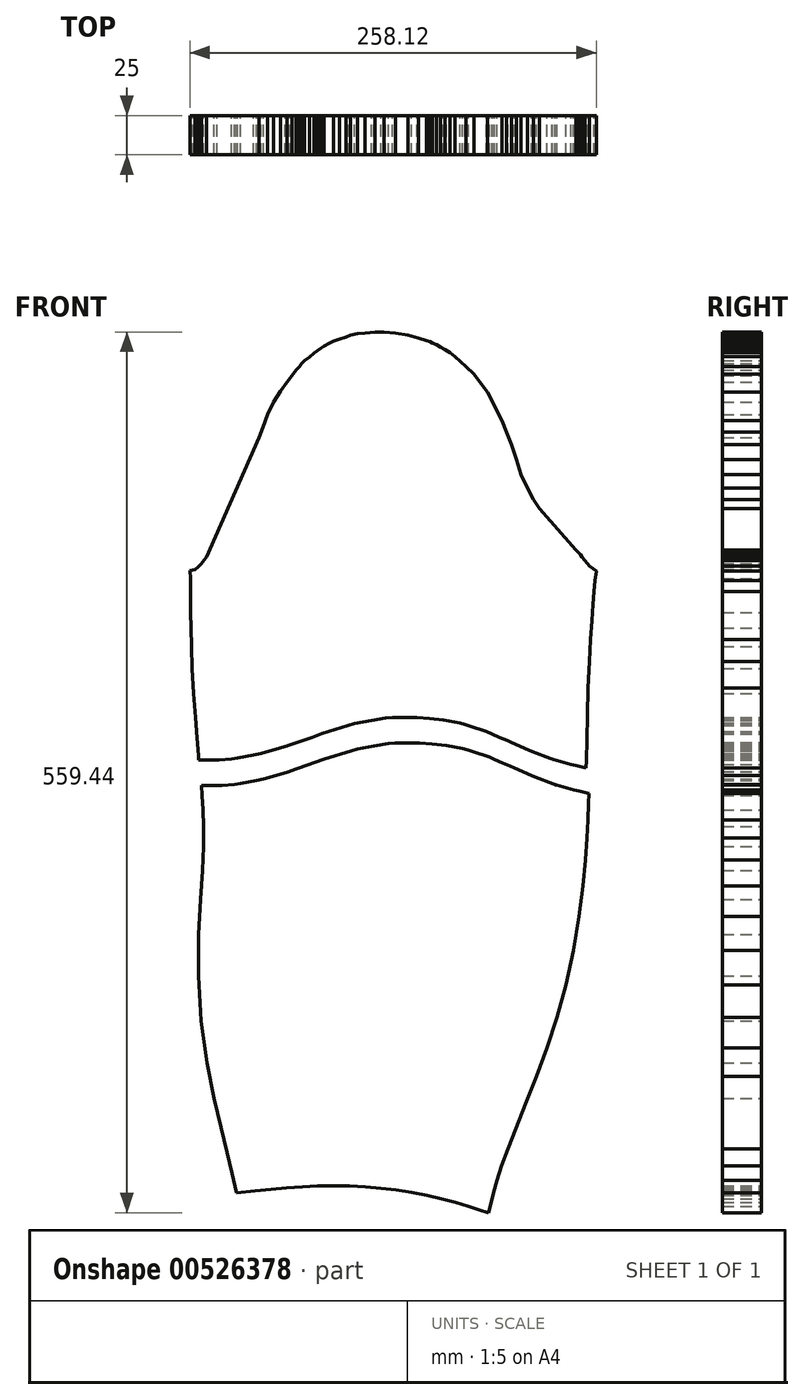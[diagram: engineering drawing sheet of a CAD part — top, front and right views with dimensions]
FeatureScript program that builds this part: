
annotation { "Feature Type Name" : "Feature", "Feature Type Description" : "" }
export const myFeature = defineFeature(function(context is Context, id is Id, definition is map)
    precondition{}
    {
        {
            var Q0;
            Q0=qCreatedBy(makeId("Front.planeOp"),FACE);
            var sketch = newSketch(context, id + "F0", { "sketchPlane" : qUnion([Q0])});
            skLineSegment(sketch, "E0", {"start": v(-129.06, 127.99) * mm, "end": v(-125.78, 128.92) * mm});
            skLineSegment(sketch, "E1", {"start": v(-125.78, 128.92) * mm, "end": v(-123.74, 130.52) * mm});
            skLineSegment(sketch, "E2", {"start": v(-123.74, 130.52) * mm, "end": v(-121.67, 132.71) * mm});
            skLineSegment(sketch, "E3", {"start": v(-121.67, 132.71) * mm, "end": v(-119.92, 134.96) * mm});
            skLineSegment(sketch, "E4", {"start": v(-119.92, 134.96) * mm, "end": v(-118.45, 136.86) * mm});
            skLineSegment(sketch, "E5", {"start": v(-118.45, 136.86) * mm, "end": v(-85.06, 212.65) * mm});
            skLineSegment(sketch, "E6", {"start": v(-85.06, 212.65) * mm, "end": v(-82.6, 219.33) * mm});
            skLineSegment(sketch, "E7", {"start": v(-82.6, 219.33) * mm, "end": v(-79.7, 227.1) * mm});
            skLineSegment(sketch, "E8", {"start": v(-79.7, 227.1) * mm, "end": v(-75.87, 235.03) * mm});
            skLineSegment(sketch, "E9", {"start": v(-75.87, 235.03) * mm, "end": v(-71.47, 242.22) * mm});
            skLineSegment(sketch, "E10", {"start": v(-71.47, 242.22) * mm, "end": v(-67.32, 247.98) * mm});
            skLineSegment(sketch, "E11", {"start": v(-67.32, 247.98) * mm, "end": v(-64.18, 252.12) * mm});
            skLineSegment(sketch, "E12", {"start": v(-64.18, 252.12) * mm, "end": v(-61.7, 255.53) * mm});
            skLineSegment(sketch, "E13", {"start": v(-61.7, 255.53) * mm, "end": v(-59.4, 257.84) * mm});
            skLineSegment(sketch, "E14", {"start": v(-59.4, 257.84) * mm, "end": v(-58.19, 259.5) * mm});
            skLineSegment(sketch, "E15", {"start": v(-58.19, 259.5) * mm, "end": v(-56.4, 261.46) * mm});
            skLineSegment(sketch, "E16", {"start": v(-56.4, 261.46) * mm, "end": v(-53.2, 263.83) * mm});
            skLineSegment(sketch, "E17", {"start": v(-53.2, 263.83) * mm, "end": v(-50.06, 266.24) * mm});
            skLineSegment(sketch, "E18", {"start": v(-50.06, 266.24) * mm, "end": v(-48.03, 267.92) * mm});
            skLineSegment(sketch, "E19", {"start": v(-48.03, 267.92) * mm, "end": v(-45.8, 269.31) * mm});
            skLineSegment(sketch, "E20", {"start": v(-45.8, 269.31) * mm, "end": v(-43.72, 270.77) * mm});
            skLineSegment(sketch, "E21", {"start": v(-43.72, 270.77) * mm, "end": v(-40.37, 272.52) * mm});
            skLineSegment(sketch, "E22", {"start": v(-40.37, 272.52) * mm, "end": v(-37.71, 273.92) * mm});
            skLineSegment(sketch, "E23", {"start": v(-37.71, 273.92) * mm, "end": v(-33.9, 275.3) * mm});
            skLineSegment(sketch, "E24", {"start": v(-33.9, 275.3) * mm, "end": v(-30.01, 276.47) * mm});
            skLineSegment(sketch, "E25", {"start": v(-30.01, 276.47) * mm, "end": v(-27.04, 277.54) * mm});
            skLineSegment(sketch, "E26", {"start": v(-27.04, 277.54) * mm, "end": v(-22.6, 278.6) * mm});
            skLineSegment(sketch, "E27", {"start": v(-22.6, 278.6) * mm, "end": v(-17.94, 279.04) * mm});
            skLineSegment(sketch, "E28", {"start": v(-17.94, 279.04) * mm, "end": v(-11.4, 279.5) * mm});
            skLineSegment(sketch, "E29", {"start": v(-11.4, 279.5) * mm, "end": v(-5.8, 279.72) * mm});
            skLineSegment(sketch, "E30", {"start": v(-5.8, 279.72) * mm, "end": v(1.6, 279.03) * mm});
            skLineSegment(sketch, "E31", {"start": v(1.6, 279.03) * mm, "end": v(9.41, 277.6) * mm});
            skLineSegment(sketch, "E32", {"start": v(9.41, 277.6) * mm, "end": v(16.28, 275.7) * mm});
            skLineSegment(sketch, "E33", {"start": v(16.28, 275.7) * mm, "end": v(21.23, 274.15) * mm});
            skLineSegment(sketch, "E34", {"start": v(21.23, 274.15) * mm, "end": v(23.5, 273.55) * mm});
            skLineSegment(sketch, "E35", {"start": v(23.5, 273.55) * mm, "end": v(25.19, 272.62) * mm});
            skLineSegment(sketch, "E36", {"start": v(25.19, 272.62) * mm, "end": v(27.5, 271.6) * mm});
            skLineSegment(sketch, "E37", {"start": v(27.5, 271.6) * mm, "end": v(30.25, 269.98) * mm});
            skLineSegment(sketch, "E38", {"start": v(30.25, 269.98) * mm, "end": v(32.91, 268.54) * mm});
            skLineSegment(sketch, "E39", {"start": v(32.91, 268.54) * mm, "end": v(36.27, 266.46) * mm});
            skLineSegment(sketch, "E40", {"start": v(36.27, 266.46) * mm, "end": v(39.3, 263.93) * mm});
            skLineSegment(sketch, "E41", {"start": v(39.3, 263.93) * mm, "end": v(46.3, 257.73) * mm});
            skLineSegment(sketch, "E42", {"start": v(46.3, 257.73) * mm, "end": v(51.38, 252.95) * mm});
            skLineSegment(sketch, "E43", {"start": v(51.38, 252.95) * mm, "end": v(55.72, 247.02) * mm});
            skLineSegment(sketch, "E44", {"start": v(55.72, 247.02) * mm, "end": v(59.84, 241.45) * mm});
            skLineSegment(sketch, "E45", {"start": v(59.84, 241.45) * mm, "end": v(69.25, 223.53) * mm});
            skLineSegment(sketch, "E46", {"start": v(69.25, 223.53) * mm, "end": v(71.89, 216.2) * mm});
            skLineSegment(sketch, "E47", {"start": v(71.89, 216.2) * mm, "end": v(75.36, 208) * mm});
            skLineSegment(sketch, "E48", {"start": v(75.36, 208) * mm, "end": v(78.39, 198.63) * mm});
            skLineSegment(sketch, "E49", {"start": v(78.39, 198.63) * mm, "end": v(81.28, 188.97) * mm});
            skLineSegment(sketch, "E50", {"start": v(81.28, 188.97) * mm, "end": v(85.37, 180.55) * mm});
            skLineSegment(sketch, "E51", {"start": v(85.37, 180.55) * mm, "end": v(89.27, 173.34) * mm});
            skLineSegment(sketch, "E52", {"start": v(89.27, 173.34) * mm, "end": v(93, 167.63) * mm});
            skLineSegment(sketch, "E53", {"start": v(93, 167.63) * mm, "end": v(116.08, 141.22) * mm});
            skLineSegment(sketch, "E54", {"start": v(116.08, 141.22) * mm, "end": v(117.67, 139.44) * mm});
            skLineSegment(sketch, "E55", {"start": v(117.67, 139.44) * mm, "end": v(118.96, 138.2) * mm});
            skLineSegment(sketch, "E56", {"start": v(118.96, 138.2) * mm, "end": v(120.13, 136.65) * mm});
            skLineSegment(sketch, "E57", {"start": v(120.13, 136.65) * mm, "end": v(121.99, 134.64) * mm});
            skLineSegment(sketch, "E58", {"start": v(121.99, 134.64) * mm, "end": v(124.73, 131.11) * mm});
            skLineSegment(sketch, "E59", {"start": v(124.73, 131.11) * mm, "end": v(129.06, 127.9) * mm});
            skLineSegment(sketch, "E60", {"start": v(129.06, 127.9) * mm, "end": v(128.28, 121.94) * mm});
            skLineSegment(sketch, "E61", {"start": v(128.28, 121.94) * mm, "end": v(127.6, 114.85) * mm});
            skLineSegment(sketch, "E62", {"start": v(127.6, 114.85) * mm, "end": v(126.92, 106.4) * mm});
            skLineSegment(sketch, "E63", {"start": v(126.92, 106.4) * mm, "end": v(126.18, 96.34) * mm});
            skLineSegment(sketch, "E64", {"start": v(126.18, 96.34) * mm, "end": v(125.4, 84.41) * mm});
            skLineSegment(sketch, "E65", {"start": v(125.4, 84.41) * mm, "end": v(124.62, 70.26) * mm});
            skLineSegment(sketch, "E66", {"start": v(124.62, 70.26) * mm, "end": v(123.94, 53.44) * mm});
            skLineSegment(sketch, "E67", {"start": v(123.94, 53.44) * mm, "end": v(123.45, 36.05) * mm});
            skLineSegment(sketch, "E68", {"start": v(123.45, 36.05) * mm, "end": v(123.1, 20.74) * mm});
            skLineSegment(sketch, "E69", {"start": v(123.1, 20.74) * mm, "end": v(122.77, 7.64) * mm});
            skLineSegment(sketch, "E70", {"start": v(122.77, 7.64) * mm, "end": v(122.6, 2.87) * mm});
            skLineSegment(sketch, "E71", {"start": v(122.6, 2.87) * mm, "end": v(116.26, 4.18) * mm});
            skLineSegment(sketch, "E72", {"start": v(116.26, 4.18) * mm, "end": v(113.1, 4.8) * mm});
            skLineSegment(sketch, "E73", {"start": v(113.1, 4.8) * mm, "end": v(102, 8.01) * mm});
            skLineSegment(sketch, "E74", {"start": v(102, 8.01) * mm, "end": v(101.15, 8.25) * mm});
            skLineSegment(sketch, "E75", {"start": v(101.15, 8.25) * mm, "end": v(100.98, 8.32) * mm});
            skLineSegment(sketch, "E76", {"start": v(100.98, 8.32) * mm, "end": v(100.06, 8.68) * mm});
            skLineSegment(sketch, "E77", {"start": v(100.06, 8.68) * mm, "end": v(88.25, 13.28) * mm});
            skLineSegment(sketch, "E78", {"start": v(88.25, 13.28) * mm, "end": v(86.15, 14.09) * mm});
            skLineSegment(sketch, "E79", {"start": v(86.15, 14.09) * mm, "end": v(75.3, 18.88) * mm});
            skLineSegment(sketch, "E80", {"start": v(75.3, 18.88) * mm, "end": v(72.52, 20.08) * mm});
            skLineSegment(sketch, "E81", {"start": v(72.52, 20.08) * mm, "end": v(67.7, 22.18) * mm});
            skLineSegment(sketch, "E82", {"start": v(67.7, 22.18) * mm, "end": v(62.7, 24.37) * mm});
            skLineSegment(sketch, "E83", {"start": v(62.7, 24.37) * mm, "end": v(59.36, 25.76) * mm});
            skLineSegment(sketch, "E84", {"start": v(59.36, 25.76) * mm, "end": v(48.53, 29.38) * mm});
            skLineSegment(sketch, "E85", {"start": v(48.53, 29.38) * mm, "end": v(45.64, 30.34) * mm});
            skLineSegment(sketch, "E86", {"start": v(45.64, 30.34) * mm, "end": v(42.36, 31.17) * mm});
            skLineSegment(sketch, "E87", {"start": v(42.36, 31.17) * mm, "end": v(32.12, 33.1) * mm});
            skLineSegment(sketch, "E88", {"start": v(32.12, 33.1) * mm, "end": v(23.04, 34.23) * mm});
            skLineSegment(sketch, "E89", {"start": v(23.04, 34.23) * mm, "end": v(15.13, 34.8) * mm});
            skLineSegment(sketch, "E90", {"start": v(15.13, 34.8) * mm, "end": v(-0.5, 34.69) * mm});
            skLineSegment(sketch, "E91", {"start": v(-0.5, 34.69) * mm, "end": v(-4.82, 34.6) * mm});
            skLineSegment(sketch, "E92", {"start": v(-4.82, 34.6) * mm, "end": v(-13.8, 32.87) * mm});
            skLineSegment(sketch, "E93", {"start": v(-13.8, 32.87) * mm, "end": v(-24.33, 30.99) * mm});
            skLineSegment(sketch, "E94", {"start": v(-24.33, 30.99) * mm, "end": v(-28.64, 29.75) * mm});
            skLineSegment(sketch, "E95", {"start": v(-28.64, 29.75) * mm, "end": v(-45.2, 24.49) * mm});
            skLineSegment(sketch, "E96", {"start": v(-45.2, 24.49) * mm, "end": v(-51.53, 22.25) * mm});
            skLineSegment(sketch, "E97", {"start": v(-51.53, 22.25) * mm, "end": v(-66.86, 16.9) * mm});
            skLineSegment(sketch, "E98", {"start": v(-66.86, 16.9) * mm, "end": v(-67.43, 16.71) * mm});
            skLineSegment(sketch, "E99", {"start": v(-67.43, 16.71) * mm, "end": v(-68.62, 16.33) * mm});
            skLineSegment(sketch, "E100", {"start": v(-68.62, 16.33) * mm, "end": v(-71.7, 15.5) * mm});
            skLineSegment(sketch, "E101", {"start": v(-71.7, 15.5) * mm, "end": v(-84, 12.04) * mm});
            skLineSegment(sketch, "E102", {"start": v(-84, 12.04) * mm, "end": v(-88.47, 11.04) * mm});
            skLineSegment(sketch, "E103", {"start": v(-88.47, 11.04) * mm, "end": v(-98.66, 9.15) * mm});
            skLineSegment(sketch, "E104", {"start": v(-98.66, 9.15) * mm, "end": v(-102.44, 8.55) * mm});
            skLineSegment(sketch, "E105", {"start": v(-102.44, 8.55) * mm, "end": v(-110.4, 7.93) * mm});
            skLineSegment(sketch, "E106", {"start": v(-110.4, 7.93) * mm, "end": v(-113.6, 7.68) * mm});
            skLineSegment(sketch, "E107", {"start": v(-113.6, 7.68) * mm, "end": v(-116.64, 7.7) * mm});
            skLineSegment(sketch, "E108", {"start": v(-116.64, 7.7) * mm, "end": v(-123.46, 7.78) * mm});
            skLineSegment(sketch, "E109", {"start": v(-123.46, 7.78) * mm, "end": v(-123.66, 10.72) * mm});
            skLineSegment(sketch, "E110", {"start": v(-123.66, 10.72) * mm, "end": v(-124.49, 21.76) * mm});
            skLineSegment(sketch, "E111", {"start": v(-124.49, 21.76) * mm, "end": v(-125.5, 34.65) * mm});
            skLineSegment(sketch, "E112", {"start": v(-125.5, 34.65) * mm, "end": v(-126.62, 50.2) * mm});
            skLineSegment(sketch, "E113", {"start": v(-126.62, 50.2) * mm, "end": v(-127.52, 66.05) * mm});
            skLineSegment(sketch, "E114", {"start": v(-127.52, 66.05) * mm, "end": v(-128.1, 79.86) * mm});
            skLineSegment(sketch, "E115", {"start": v(-128.1, 79.86) * mm, "end": v(-128.43, 91.56) * mm});
            skLineSegment(sketch, "E116", {"start": v(-128.43, 91.56) * mm, "end": v(-128.6, 101.4) * mm});
            skLineSegment(sketch, "E117", {"start": v(-128.6, 101.4) * mm, "end": v(-128.65, 109.84) * mm});
            skLineSegment(sketch, "E118", {"start": v(-128.65, 109.84) * mm, "end": v(-128.7, 116.9) * mm});
            skLineSegment(sketch, "E119", {"start": v(-128.7, 116.9) * mm, "end": v(-128.76, 122.9) * mm});
            skLineSegment(sketch, "E120", {"start": v(-128.76, 122.9) * mm, "end": v(-129.06, 127.99) * mm});
            skLineSegment(sketch, "E121", {"start": v(-87.7, -265.91) * mm, "end": v(-99.36, -267.16) * mm});
            skLineSegment(sketch, "E122", {"start": v(-99.36, -267.16) * mm, "end": v(-102.24, -254.86) * mm});
            skLineSegment(sketch, "E123", {"start": v(-102.24, -254.86) * mm, "end": v(-105.54, -241.28) * mm});
            skLineSegment(sketch, "E124", {"start": v(-105.54, -241.28) * mm, "end": v(-109.4, -225.58) * mm});
            skLineSegment(sketch, "E125", {"start": v(-109.4, -225.58) * mm, "end": v(-113.8, -207) * mm});
            skLineSegment(sketch, "E126", {"start": v(-113.8, -207) * mm, "end": v(-118.22, -184.67) * mm});
            skLineSegment(sketch, "E127", {"start": v(-118.22, -184.67) * mm, "end": v(-121.8, -157.96) * mm});
            skLineSegment(sketch, "E128", {"start": v(-121.8, -157.96) * mm, "end": v(-123.6, -129.31) * mm});
            skLineSegment(sketch, "E129", {"start": v(-123.6, -129.31) * mm, "end": v(-123.45, -102.96) * mm});
            skLineSegment(sketch, "E130", {"start": v(-123.45, -102.96) * mm, "end": v(-122.29, -80.62) * mm});
            skLineSegment(sketch, "E131", {"start": v(-122.29, -80.62) * mm, "end": v(-121.14, -62.26) * mm});
            skLineSegment(sketch, "E132", {"start": v(-121.14, -62.26) * mm, "end": v(-120.48, -47.14) * mm});
            skLineSegment(sketch, "E133", {"start": v(-120.48, -47.14) * mm, "end": v(-120.42, -34.55) * mm});
            skLineSegment(sketch, "E134", {"start": v(-120.42, -34.55) * mm, "end": v(-120.76, -23.9) * mm});
            skLineSegment(sketch, "E135", {"start": v(-120.76, -23.9) * mm, "end": v(-121.24, -14.8) * mm});
            skLineSegment(sketch, "E136", {"start": v(-121.24, -14.8) * mm, "end": v(-121.67, -8.4) * mm});
            skLineSegment(sketch, "E137", {"start": v(-121.67, -8.4) * mm, "end": v(-114.85, -8.49) * mm});
            skLineSegment(sketch, "E138", {"start": v(-114.85, -8.49) * mm, "end": v(-111.81, -8.5) * mm});
            skLineSegment(sketch, "E139", {"start": v(-111.81, -8.5) * mm, "end": v(-108.62, -8.26) * mm});
            skLineSegment(sketch, "E140", {"start": v(-108.62, -8.26) * mm, "end": v(-100.65, -7.64) * mm});
            skLineSegment(sketch, "E141", {"start": v(-100.65, -7.64) * mm, "end": v(-96.86, -7.03) * mm});
            skLineSegment(sketch, "E142", {"start": v(-96.86, -7.03) * mm, "end": v(-86.68, -5.15) * mm});
            skLineSegment(sketch, "E143", {"start": v(-86.68, -5.15) * mm, "end": v(-82.2, -4.15) * mm});
            skLineSegment(sketch, "E144", {"start": v(-82.2, -4.15) * mm, "end": v(-69.9, -0.7) * mm});
            skLineSegment(sketch, "E145", {"start": v(-69.9, -0.7) * mm, "end": v(-66.82, 0.15) * mm});
            skLineSegment(sketch, "E146", {"start": v(-66.82, 0.15) * mm, "end": v(-65.63, 0.53) * mm});
            skLineSegment(sketch, "E147", {"start": v(-65.63, 0.53) * mm, "end": v(-65.07, 0.72) * mm});
            skLineSegment(sketch, "E148", {"start": v(-65.07, 0.72) * mm, "end": v(-49.74, 6.07) * mm});
            skLineSegment(sketch, "E149", {"start": v(-49.74, 6.07) * mm, "end": v(-43.4, 8.3) * mm});
            skLineSegment(sketch, "E150", {"start": v(-43.4, 8.3) * mm, "end": v(-26.85, 13.57) * mm});
            skLineSegment(sketch, "E151", {"start": v(-26.85, 13.57) * mm, "end": v(-22.54, 14.8) * mm});
            skLineSegment(sketch, "E152", {"start": v(-22.54, 14.8) * mm, "end": v(-12, 16.69) * mm});
            skLineSegment(sketch, "E153", {"start": v(-12, 16.69) * mm, "end": v(-3.03, 18.4) * mm});
            skLineSegment(sketch, "E154", {"start": v(-3.03, 18.4) * mm, "end": v(1.3, 18.5) * mm});
            skLineSegment(sketch, "E155", {"start": v(1.3, 18.5) * mm, "end": v(16.93, 18.62) * mm});
            skLineSegment(sketch, "E156", {"start": v(16.93, 18.62) * mm, "end": v(24.83, 18.05) * mm});
            skLineSegment(sketch, "E157", {"start": v(24.83, 18.05) * mm, "end": v(33.92, 16.92) * mm});
            skLineSegment(sketch, "E158", {"start": v(33.92, 16.92) * mm, "end": v(44.15, 14.98) * mm});
            skLineSegment(sketch, "E159", {"start": v(44.15, 14.98) * mm, "end": v(47.44, 14.16) * mm});
            skLineSegment(sketch, "E160", {"start": v(47.44, 14.16) * mm, "end": v(50.33, 13.2) * mm});
            skLineSegment(sketch, "E161", {"start": v(50.33, 13.2) * mm, "end": v(61.15, 9.58) * mm});
            skLineSegment(sketch, "E162", {"start": v(61.15, 9.58) * mm, "end": v(64.49, 8.19) * mm});
            skLineSegment(sketch, "E163", {"start": v(64.49, 8.19) * mm, "end": v(69.5, 6) * mm});
            skLineSegment(sketch, "E164", {"start": v(69.5, 6) * mm, "end": v(74.32, 3.9) * mm});
            skLineSegment(sketch, "E165", {"start": v(74.32, 3.9) * mm, "end": v(77.09, 2.7) * mm});
            skLineSegment(sketch, "E166", {"start": v(77.09, 2.7) * mm, "end": v(87.94, -2.1) * mm});
            skLineSegment(sketch, "E167", {"start": v(87.94, -2.1) * mm, "end": v(90.05, -2.9) * mm});
            skLineSegment(sketch, "E168", {"start": v(90.05, -2.9) * mm, "end": v(101.85, -7.5) * mm});
            skLineSegment(sketch, "E169", {"start": v(101.85, -7.5) * mm, "end": v(102.77, -7.87) * mm});
            skLineSegment(sketch, "E170", {"start": v(102.77, -7.87) * mm, "end": v(102.94, -7.93) * mm});
            skLineSegment(sketch, "E171", {"start": v(102.94, -7.93) * mm, "end": v(103.8, -8.18) * mm});
            skLineSegment(sketch, "E172", {"start": v(103.8, -8.18) * mm, "end": v(114.9, -11.38) * mm});
            skLineSegment(sketch, "E173", {"start": v(114.9, -11.38) * mm, "end": v(118.05, -12) * mm});
            skLineSegment(sketch, "E174", {"start": v(118.05, -12) * mm, "end": v(124.4, -13.32) * mm});
            skLineSegment(sketch, "E175", {"start": v(124.4, -13.32) * mm, "end": v(124.2, -19.73) * mm});
            skLineSegment(sketch, "E176", {"start": v(124.2, -19.73) * mm, "end": v(123.76, -30.22) * mm});
            skLineSegment(sketch, "E177", {"start": v(123.76, -30.22) * mm, "end": v(123.13, -41.87) * mm});
            skLineSegment(sketch, "E178", {"start": v(123.13, -41.87) * mm, "end": v(122.13, -55.73) * mm});
            skLineSegment(sketch, "E179", {"start": v(122.13, -55.73) * mm, "end": v(120.58, -72.16) * mm});
            skLineSegment(sketch, "E180", {"start": v(120.58, -72.16) * mm, "end": v(118.1, -91.62) * mm});
            skLineSegment(sketch, "E181", {"start": v(118.1, -91.62) * mm, "end": v(114.57, -113.12) * mm});
            skLineSegment(sketch, "E182", {"start": v(114.57, -113.12) * mm, "end": v(109.97, -134.97) * mm});
            skLineSegment(sketch, "E183", {"start": v(109.97, -134.97) * mm, "end": v(104.24, -155.86) * mm});
            skLineSegment(sketch, "E184", {"start": v(104.24, -155.86) * mm, "end": v(97.88, -175.22) * mm});
            skLineSegment(sketch, "E185", {"start": v(97.88, -175.22) * mm, "end": v(90.96, -193.3) * mm});
            skLineSegment(sketch, "E186", {"start": v(90.96, -193.3) * mm, "end": v(84.09, -210.56) * mm});
            skLineSegment(sketch, "E187", {"start": v(84.09, -210.56) * mm, "end": v(78, -226.2) * mm});
            skLineSegment(sketch, "E188", {"start": v(78, -226.2) * mm, "end": v(72.87, -239.23) * mm});
            skLineSegment(sketch, "E189", {"start": v(72.87, -239.23) * mm, "end": v(68.92, -250.06) * mm});
            skLineSegment(sketch, "E190", {"start": v(68.92, -250.06) * mm, "end": v(66.07, -259.26) * mm});
            skLineSegment(sketch, "E191", {"start": v(66.07, -259.26) * mm, "end": v(63.86, -267.16) * mm});
            skLineSegment(sketch, "E192", {"start": v(63.86, -267.16) * mm, "end": v(62.1, -273.9) * mm});
            skLineSegment(sketch, "E193", {"start": v(62.1, -273.9) * mm, "end": v(60.62, -279.72) * mm});
            skLineSegment(sketch, "E194", {"start": v(60.62, -279.72) * mm, "end": v(54.7, -277.8) * mm});
            skLineSegment(sketch, "E195", {"start": v(54.7, -277.8) * mm, "end": v(47.86, -275.62) * mm});
            skLineSegment(sketch, "E196", {"start": v(47.86, -275.62) * mm, "end": v(39.78, -273.22) * mm});
            skLineSegment(sketch, "E197", {"start": v(39.78, -273.22) * mm, "end": v(30.7, -270.84) * mm});
            skLineSegment(sketch, "E198", {"start": v(30.7, -270.84) * mm, "end": v(21.4, -268.69) * mm});
            skLineSegment(sketch, "E199", {"start": v(21.4, -268.69) * mm, "end": v(11.78, -266.76) * mm});
            skLineSegment(sketch, "E200", {"start": v(11.78, -266.76) * mm, "end": v(1.94, -265.26) * mm});
            skLineSegment(sketch, "E201", {"start": v(1.94, -265.26) * mm, "end": v(-7.7, -264.14) * mm});
            skLineSegment(sketch, "E202", {"start": v(-7.7, -264.14) * mm, "end": v(-17.62, -263.34) * mm});
            skLineSegment(sketch, "E203", {"start": v(-17.62, -263.34) * mm, "end": v(-27.55, -262.83) * mm});
            skLineSegment(sketch, "E204", {"start": v(-27.55, -262.83) * mm, "end": v(-37.62, -262.62) * mm});
            skLineSegment(sketch, "E205", {"start": v(-37.62, -262.62) * mm, "end": v(-47.84, -262.75) * mm});
            skLineSegment(sketch, "E206", {"start": v(-47.84, -262.75) * mm, "end": v(-57.63, -263.2) * mm});
            skLineSegment(sketch, "E207", {"start": v(-57.63, -263.2) * mm, "end": v(-67.69, -263.95) * mm});
            skLineSegment(sketch, "E208", {"start": v(-67.69, -263.95) * mm, "end": v(-77.64, -264.89) * mm});
            skLineSegment(sketch, "E209", {"start": v(-77.64, -264.89) * mm, "end": v(-87.7, -265.91) * mm});
            skSolve(sketch);
        }
        {
            var Q0;
            Q0=makeQuery(id+"F0.imprint","IMPRINT",FACE,{"disambiguationData":[TD([[makeQuery(id+"F0.imprint","IMPRINT",EDGE,{"derivedFrom":sQuery(id+"F0.wireOp",EDGE,"E121")}),-1.0]])]});
            var Q1;
            Q1=makeQuery(id+"F0.imprint","IMPRINT",FACE,{"disambiguationData":[TD([[makeQuery(id+"F0.imprint","IMPRINT",EDGE,{"derivedFrom":sQuery(id+"F0.wireOp",EDGE,"E0")}),-1.0]])]});
            extrude(context, id + "F1", {"entities" : qUnion([Q0, Q1]), "depth" : 25 * mm, "offsetDistance" : 25 * mm});
        }
    });
